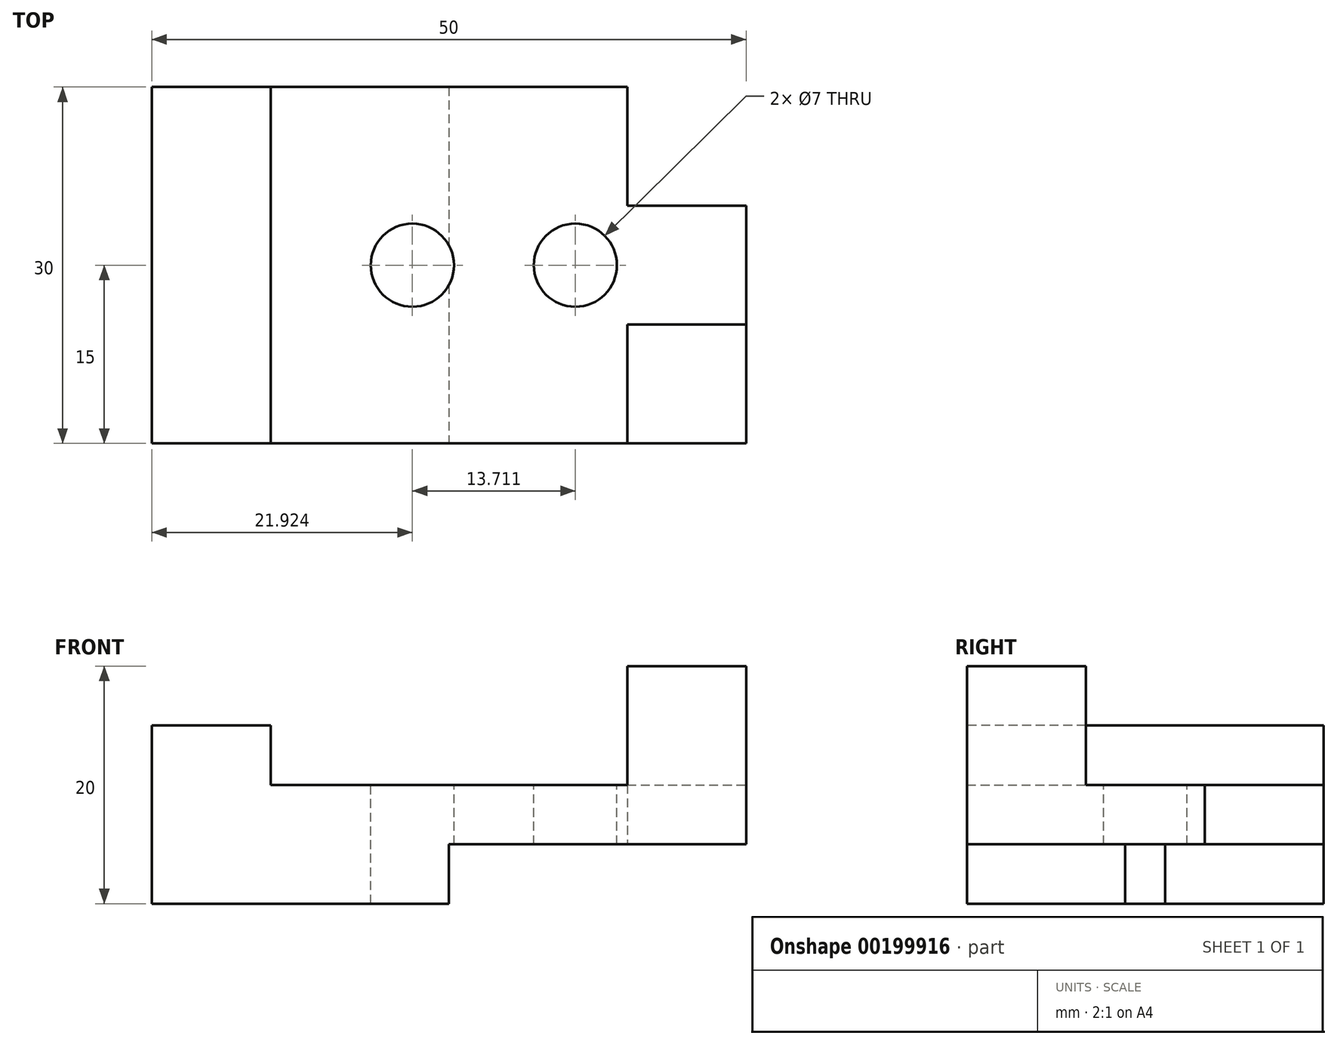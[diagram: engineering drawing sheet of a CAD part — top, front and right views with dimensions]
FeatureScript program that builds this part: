
annotation { "Feature Type Name" : "Feature", "Feature Type Description" : "" }
export const myFeature = defineFeature(function(context is Context, id is Id, definition is map)
    precondition{}
    {
        {
            var Q0;
            Q0=qCreatedBy(makeId("Top.planeOp"),FACE);
            var sketch = newSketch(context, id + "F0", { "sketchPlane" : qUnion([Q0])});
            skLineSegment(sketch, "E0", {"start": v(-28.78, 0) * mm, "end": v(21.22, 0) * mm});
            skLineSegment(sketch, "E1", {"start": v(21.22, 0) * mm, "end": v(21.22, -30) * mm});
            skLineSegment(sketch, "E2", {"start": v(-28.78, 0) * mm, "end": v(-28.78, -30) * mm});
            skLineSegment(sketch, "E3", {"start": v(-28.78, -30) * mm, "end": v(21.22, -30) * mm});
            skLineSegment(sketch, "E4", {"start": v(-3.78, 0) * mm, "end": v(-3.78, -30) * mm});
            skLineSegment(sketch, "E5", {"start": v(-18.78, 0) * mm, "end": v(-28.78, 0) * mm});
            skLineSegment(sketch, "E6", {"start": v(-18.78, 0) * mm, "end": v(-18.78, -30) * mm});
            skLineSegment(sketch, "E7", {"start": v(11.22, 0) * mm, "end": v(21.22, 0) * mm});
            skLineSegment(sketch, "E8", {"start": v(11.22, 0) * mm, "end": v(11.22, -10) * mm});
            skLineSegment(sketch, "E9", {"start": v(11.22, -10) * mm, "end": v(21.22, -10) * mm});
            skLineSegment(sketch, "E10", {"start": v(11.22, -30) * mm, "end": v(11.22, -20) * mm});
            skLineSegment(sketch, "E11", {"start": v(21.22, -20) * mm, "end": v(11.22, -20) * mm});
            skSolve(sketch);
        }
        {
            var Q0;
            {var subQ0=sQuery(id+"F0.wireOp",EDGE,"E2");Q0=makeQuery(id+"F0.imprint","IMPRINT",FACE,{"disambiguationData":[TD([[makeQuery(id+"F0.imprint","IMPRINT",EDGE,{"derivedFrom":subQ0}),1.0]])]});}
            extrude(context, id + "F1", {"entities" : qUnion([Q0]), "depth" : 15 * mm});
        }
        {
            var Q0;
            {var subQ2=sQuery(id+"F0.wireOp",EDGE,"E4");Q0=makeQuery(id+"F0.imprint","IMPRINT",FACE,{"disambiguationData":[TD([[makeQuery(id+"F0.imprint","IMPRINT",EDGE,{"derivedFrom":subQ2}),-1.0]])]});}
            var Q1;
            {var subQ0=sQuery(id+"F0.wireOp",EDGE,"E4");Q1=makeQuery(id+"F0.imprint","IMPRINT",FACE,{"disambiguationData":[TD([[makeQuery(id+"F0.imprint","IMPRINT",EDGE,{"derivedFrom":subQ0}),1.0]])]});}
            extrude(context, id + "F2", {"entities" : qUnion([Q0, Q1]), "operationType" : NewBodyOperationType.ADD, "depth" : 10 * mm});
        }
        {
            var Q0;
            {var subQ4=sQuery(id+"F0.wireOp",EDGE,"E10");Q0=makeQuery(id+"F0.imprint","IMPRINT",FACE,{"disambiguationData":[TD([[makeQuery(id+"F0.imprint","IMPRINT",EDGE,{"derivedFrom":subQ4}),-1.0]])]});}
            var Q1;
            {var subQ0=sQuery(id+"F0.wireOp",EDGE,"E7");Q1=makeQuery(id+"F0.imprint","IMPRINT",FACE,{"disambiguationData":[TD([[makeQuery(id+"F0.imprint","IMPRINT",EDGE,{"derivedFrom":subQ0}),-1.0]])]});}
            extrude(context, id + "F3", {"entities" : qUnion([Q0, Q1]), "operationType" : NewBodyOperationType.ADD, "depth" : 20 * mm});
        }
        {
            var Q0;
            {var subQ0=sQuery(id+"F0.wireOp",EDGE,"E4");Q0=makeQuery(id+"F0.imprint","IMPRINT",FACE,{"disambiguationData":[TD([[makeQuery(id+"F0.imprint","IMPRINT",EDGE,{"derivedFrom":subQ0}),1.0]])]});}
            var Q1;
            {var subQ4=sQuery(id+"F0.wireOp",EDGE,"E10");Q1=makeQuery(id+"F0.imprint","IMPRINT",FACE,{"disambiguationData":[TD([[makeQuery(id+"F0.imprint","IMPRINT",EDGE,{"derivedFrom":subQ4}),-1.0]])]});}
            var Q2;
            {var subQ0=sQuery(id+"F0.wireOp",EDGE,"E7");Q2=makeQuery(id+"F0.imprint","IMPRINT",FACE,{"disambiguationData":[TD([[makeQuery(id+"F0.imprint","IMPRINT",EDGE,{"derivedFrom":subQ0}),-1.0]])]});}
            extrude(context, id + "F4", {"entities" : qUnion([Q0, Q1, Q2]), "operationType" : NewBodyOperationType.REMOVE, "depth" : 5 * mm});
        }
        {
            var Q0;
            Q0=makeQuery(id+"F2.opExtrude","CAP_FACE",FACE,{"disambiguationData":[OSD([sQuery(id+"F0.wireOp",EDGE,"E0"),sQuery(id+"F0.wireOp",EDGE,"E1"),sQuery(id+"F0.wireOp",EDGE,"E3"),sQuery(id+"F0.wireOp",EDGE,"E6"),sQuery(id+"F0.wireOp",EDGE,"E8"),sQuery(id+"F0.wireOp",EDGE,"E9"),sQuery(id+"F0.wireOp",EDGE,"E10"),sQuery(id+"F0.wireOp",EDGE,"E11")])],"isStart":false});
            var sketch = newSketch(context, id + "F5", { "sketchPlane" : qUnion([Q0])});
            skLineSegment(sketch, "E12", {"start": v(21.22, -15) * mm, "end": v(-6.86, -15) * mm});
            skCircle(sketch, "E13", {"center": v(-6.86, -15) * mm, "radius": 3.5 * mm});
            skLineSegment(sketch, "E14", {"start": v(0, 0) * mm, "end": v(0, -30) * mm, "construction": true});
            skCircle(sketch, "E15.MirrorC", {"center": v(6.86, -15) * mm, "radius": 3.5 * mm});
            skSolve(sketch);
        }
        {
            var Q0;
            Q0 = qSketchRegion(id + "F5", true);
            extrude(context, id + "F6", {"entities" : qUnion([Q0]), "operationType" : NewBodyOperationType.REMOVE, "oppositeDirection" : true, "depth" : 10 * mm});
        }
    });
